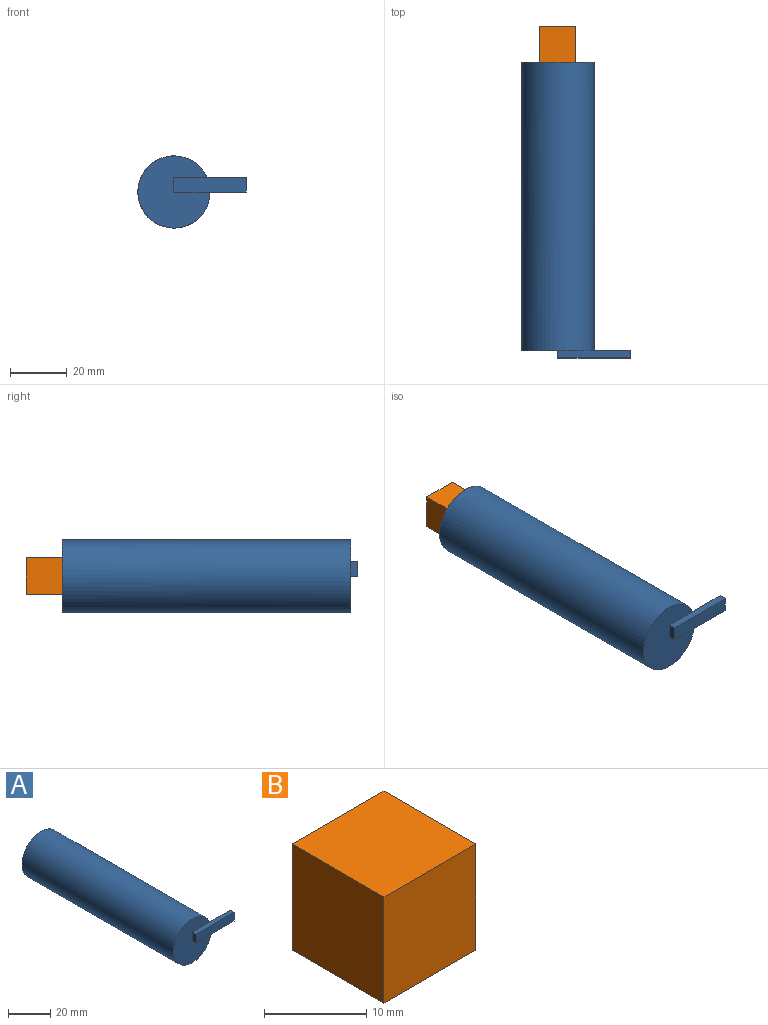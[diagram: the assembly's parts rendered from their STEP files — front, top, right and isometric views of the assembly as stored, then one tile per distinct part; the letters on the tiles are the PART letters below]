
ASSEMBLY  parts=2 mates=1
PART A: 9 faces, bbox 38.1x104.1x25.4 mm
  f0: plane 25.4x25.4mm, normal (0,-1,0), area 444mm2, adj f1,f4,f5,f6
  f1: cylinder r=12.7mm len=101.6mm, axis (0,1,0), area 8107.3mm2, adj f0,f2,f3
  f2: plane 25.4x25.4mm, normal (0,1,0), area 506.7mm2, adj f1
  f3: plane 13.76x5.08mm, normal (0,1,0), area 66.3mm2, adj f1,f4,f6,f7
  f4: plane 25.4x2.54mm, normal (0,0,1), area 64.5mm2, adj f0,f3,f5,f7,f8
  f5: plane 5.08x2.54mm, normal (-1,0,0), area 12.9mm2, adj f0,f4,f6,f8
  f6: plane 25.4x2.54mm, normal (0,0,-1), area 64.5mm2, adj f0,f3,f5,f7,f8
  f7: plane 5.08x2.54mm, normal (1,0,0), area 12.9mm2, adj f3,f4,f6,f8
  f8: plane 25.4x5.08mm, normal (0,-1,0), area 129mm2, adj f4,f5,f6,f7
PART B: 6 faces, bbox 12.7x12.7x12.7 mm
  f0: plane 12.7x12.7mm, normal (0,0,-1), area 161.3mm2, adj f1,f3,f4,f5
  f1: plane 12.7x12.7mm, normal (1,0,0), area 161.3mm2, adj f0,f2,f4,f5
  f2: plane 12.7x12.7mm, normal (0,0,1), area 161.3mm2, adj f1,f3,f4,f5
  f3: plane 12.7x12.7mm, normal (-1,0,0), area 161.3mm2, adj f0,f2,f4,f5
  f4: plane 12.7x12.7mm, normal (0,-1,0), area 161.3mm2, adj f0,f1,f2,f3
  f5: plane 12.7x12.7mm, normal (0,1,0), area 161.3mm2, adj f0,f1,f2,f3
PLACE A t=(-15.09,31.46,-23.35)mm
PLACE B rot(axis=(1,0,0),180deg) t=(-15.09,31.46,5.22)mm
MATE slider B.f5 <-> A.f1  axis (0,-1,0) through (-15.09,31.46,-23.35)mm
